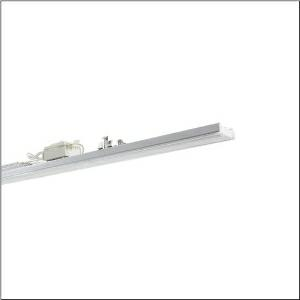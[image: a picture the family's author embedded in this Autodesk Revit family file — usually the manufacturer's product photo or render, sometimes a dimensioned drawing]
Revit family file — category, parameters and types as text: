
# Revit family: licross_21_recessed_mo_52te12dv6fxg3s
name_source: partatom
category: Lighting Fixtures
units: mm (PartAtom-declared; Revit-internal decimal feet)

## family parameters
Cut with Voids When Loaded = No
Host = Face
Light Source = No
Part Type = Normal
Room Calculation Point = No
Round Connector Dimension = Use Diameter
Shared = No

## types (1)
- --- (1 x LED, 920 lm, 5.5 W, 6500K)
    Apparent Load = 6 VA
    CIE Flux Codes = 72 92 99 100 100
    Color Rendering = 80
    Color Temperature = 6500K
    Default Elevation = 1800 mm
    Description = Licross 21 Recessed MO, luminaire insert, of sheet steel, galvanised, coil coated, white, length: 2.250mm, width: 66mm, height: 67mm, LED rated luminous flux: 15.000lm, light colour: 865, SDCM (Standard Deviation of Colour Matching)MacAdam ≤ 3 SDCM (initial), control gear: DALI 2 (for two DALI lines), with plug, 6-pole, with phase selection, for trunking rail, 14-core, mains connection: 220..240V, AC, 50/60Hz, rated input power: 89W, for trunking rail, 14-core, internal wiring halogen-free, for emergency light function, converter,control gear: single battery element, battery: LiFePO4, 9Ah, primary optical cover: cover, of PMMA, light emission: direct distribution, primary light characteristic: symmetric, protection rating (complete): IP54, insulation class (complete): insulation class I (protective earthing), certification: CE, ENEC, VDE, UKCA, protection symbol: D if used in an environment with non-conductive dust loads with corresponding accessories, impact resistance: IK06, permissible ambient temperature for indoor applications: +5..+35°C, standard: EN 60598-2-22, LABS conformity tested according to VDMA 24364:2018-05, reducing of maximum allowable ambient temperature of 5°C with ceiling mounting, corresponds to IFS (International Featured Standards) requirements for safety and quality in the food industry, The light source and the operating device comply with the requirements of the Ecodesign Regulation (EU) 2019/2020 and are replaceable in accordance with this regulation, packaging unit: 1 piece
    Height = 58 mm
    Lamp = 1 x LED
    Lamp Light Flux = 920 lm
    Lamp Power = 5.5 W
    Lamp count = 1
    Length = 2250 mm
    Luminous efficacy = 167 lm/W
    Manufacturer = Siteco
    ModVariant = No
    Model = 52TE12DV6FXG3S
    Mounting Place = Ceiling
    Mounting Type = Pendant
    Number of Poles = 1
    OnlyDefault = Yes
    Power Factor = 1
    Product Name = Licross 21 Recessed MO
    Product group = luminaire insert | ceiling pendant
    ProductGroupID = 901
    Protection Class = Protection class I
    Protection Degree = IP 54
    RLX_Detail_Level = 1
    RLX_Emergency_Light_Flux = 0 lm
    RLX_Emergency_Type = 0
    RLX_Emergency_Type_DB = No
    RlxData = <blob elided: 30225 chars, md5=154339d9>
    Socket = socket
    Standby Power = 0 W
    System Light Flux = 920 lm
    System Power = 6 W
    Type Comments = : DC mode (central or group accumulator) initial emergency light level
    Type Image = l_1296930.jpg
    URL = http://relux.com
    VarID = @adj_085345
    Voltage = 0 V
    Weight = 0.00 kg
    Width = 66 mm

## geometry (parser evidence)
native form markers: Blend x4, Sweep x9
no freeform markers — native parametric forms only
